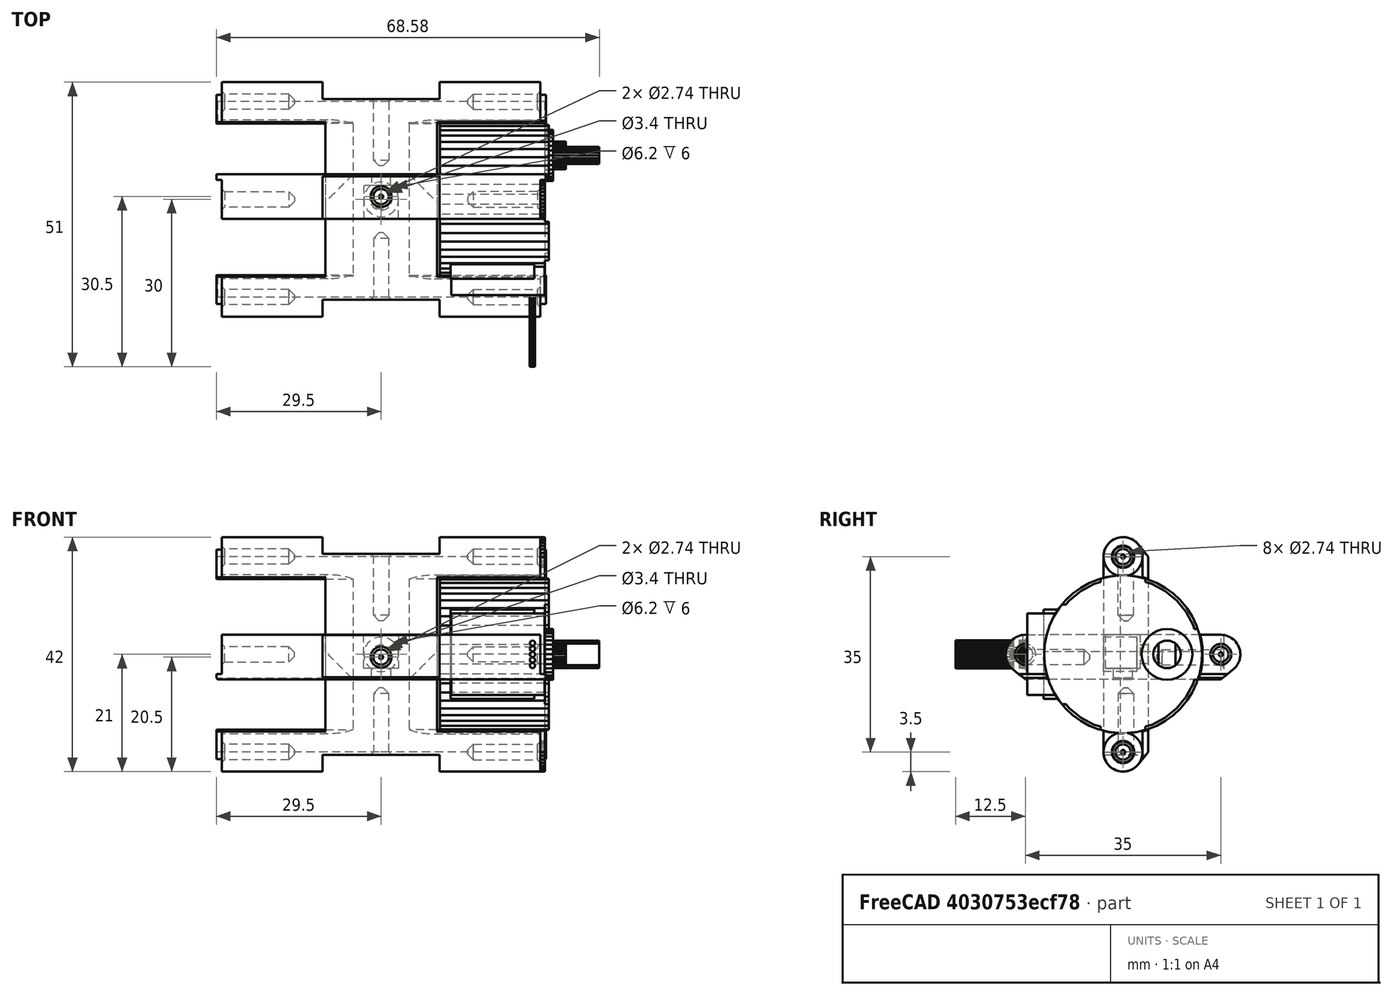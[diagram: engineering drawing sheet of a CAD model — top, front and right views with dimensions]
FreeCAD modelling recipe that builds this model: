
FCSTD DOCUMENT  (FreeCAD 0.17R10654 (Git))
Label: motor-bracket-ng
License: The MIT License
LicenseURL: http://opensource.org/licenses/MIT
objects: Sketcher::SketchObject×9, PartDesign::Pocket×8, PartDesign::Chamfer×3, PartDesign::Body×2, Part::FeaturePython×2, Part::Feature×1, PartDesign::Pad×1, App::DocumentObjectGroup×1, Mesh::Feature×1, Part::Mirroring×1, Part::MultiFuse×1, App::Part×1, Part::Chamfer×1
note: 38 computed .brp shape members not serialized (recipe doc carries the construction recipe); baked Part::Feature solids carry a one-line shape summary decoded from their .brp

FEATURE [Part::Feature] Part__Feature  label="stepper-motor"
  Placement = pos=(19.925,0,0) rot=(0.57735,0.57735,0.57735;2.0944rad)
  shape: bbox 28.55 x 44.13 x 42 mm, 425 faces (baked)
FEATURE [Sketcher::SketchObject] Sketch  label="bracket-sketch"
  MapMode = 5
  Placement = pos=(0,0,0) rot=(0.57735,0.57735,0.57735;2.0944rad)
  Support = -> [YZ_Plane001]
  sketch-geometry (6):
    g0: ArcOfCircle CenterX=0 CenterY=17.5 CenterZ=0 NormalX=0 NormalY=0 NormalZ=1 Radius=3.5 StartAngle=0.679674 EndAngle=3.14159
    g1: ArcOfCircle CenterX=0 CenterY=-17.5 CenterZ=0 NormalX=0 NormalY=0 NormalZ=1 Radius=3.5 StartAngle=3.14159 EndAngle=5.60352
    g2: LineSegment StartX=-3.5 StartY=17.5 StartZ=0 EndX=-3.5 EndY=-17.5 EndZ=0
    g3: LineSegment StartX=4.5 StartY=17.5 StartZ=0 EndX=4.5 EndY=-17.5 EndZ=0
    g4: LineSegment StartX=4.5 StartY=17.5 StartZ=0 EndX=2.72222 EndY=19.6999 EndZ=0
    g5: LineSegment StartX=2.72223 StartY=-19.6999 StartZ=0 EndX=4.5 EndY=-17.5 EndZ=0
  constraints (19):
    c: Tangent(g0,g2)
    c: Tangent(g1,g2)
    c: Coincident(g0,g2)
    c: Coincident(g2,g1)
    c: Vertical(g2)
    c: Radius(g1) = 3.5
    c: PointOnObject(g1,g-2)
    c: DistanceY(g0,g1) = -35
    c: Symmetric(g1,g0,g-1)
    c: Vertical(g3)
    c: Coincident(g3,g4)
    c: Coincident(g0,g4)
    c: Tangent(g0,g4)
    c: DistanceX(g3,g1) = -8
    c: DistanceY(g3) = -35
    c: Symmetric(g3,g3,g-1)
    c: Coincident(g5,g1)
    c: Coincident(g5,g3)
    c: Tangent(g1,g5)
FEATURE [PartDesign::Pad] Pad  label="bracket-pad"
  Length = 29.5
  Length2 = 100
  Placement = pos=(0,0,0) rot=(0.57735,0.57735,0.57735;2.0944rad)
  Profile = -> Sketch
  Type = 0
FEATURE [Sketcher::SketchObject] Sketch001  label="motor-sketch"
  MapMode = 5
  Placement = pos=(29.5,0,0) rot=(0.57735,0.57735,0.57735;2.0944rad)
  Support = -> [Pad]
  sketch-geometry (1):
    g0: Circle CenterX=0 CenterY=0 CenterZ=0 NormalX=0 NormalY=0 NormalZ=1 Radius=14.25
  constraints (2):
    c: Coincident(g0,g-1)
    c: Radius(g0) = 14.25
FEATURE [PartDesign::Pocket] Pocket  label="motor-pocket"
  BaseFeature = -> Pad
  Length = 19.5
  Placement = pos=(0,0,0) rot=(0.57735,0.57735,0.57735;2.0944rad)
  Profile = -> Sketch001
  Type = 0
FEATURE [Sketcher::SketchObject] Sketch002  label="motor-screw-holes-sketch"
  MapMode = 5
  Placement = pos=(29.5,0,0) rot=(0.57735,0.57735,0.57735;2.0944rad)
  Support = -> [Pocket]
  sketch-geometry (2):
    g0: Circle CenterX=0 CenterY=-17.5 CenterZ=0 NormalX=0 NormalY=0 NormalZ=1 Radius=1.37
    g1: Circle CenterX=0 CenterY=17.5 CenterZ=0 NormalX=0 NormalY=0 NormalZ=1 Radius=1.37
  constraints (6):
    c: PointOnObject(g0,g-2)
    c: DistanceY(g-1,g0) = -17.5
    c: Radius(g0) = 1.37
    c: PointOnObject(g1,g-2)
    c: DistanceY(g-1,g1) = 17.5
    c: Radius(g1) = 1.37
FEATURE [PartDesign::Pocket] Pocket001  label="motor-screw-holes-pocket"
  BaseFeature = -> Pocket
  Length = 14
  Placement = pos=(0,0,0) rot=(0.57735,0.57735,0.57735;2.0944rad)
  Profile = -> Sketch002
  Type = 0
FEATURE [Sketcher::SketchObject] Sketch003  label="recess-sketch"
  MapMode = 5
  Placement = pos=(0,-3.5,0) rot=(0.57735,0.57735,-0.57735;2.0944rad)
  Support = -> [Pocket001]
  sketch-geometry (8):
    g0: LineSegment StartX=-22 StartY=10.5 StartZ=0 EndX=-18 EndY=10.5 EndZ=0
    g1: LineSegment StartX=-18 StartY=10.5 StartZ=0 EndX=-18 EndY=0 EndZ=0
    g2: LineSegment StartX=-18 StartY=0 StartZ=0 EndX=-22 EndY=0 EndZ=0
    g3: LineSegment StartX=-22 StartY=0 StartZ=0 EndX=-22 EndY=10.5 EndZ=0
    g4: LineSegment StartX=18 StartY=10.5 StartZ=0 EndX=22 EndY=10.5 EndZ=0
    g5: LineSegment StartX=22 StartY=10.5 StartZ=0 EndX=22 EndY=0 EndZ=0
    g6: LineSegment StartX=22 StartY=0 StartZ=0 EndX=18 EndY=0 EndZ=0
    g7: LineSegment StartX=18 StartY=0 StartZ=0 EndX=18 EndY=10.5 EndZ=0
  constraints (24):
    c: Coincident(g0,g1)
    c: Coincident(g1,g2)
    c: Coincident(g2,g3)
    c: Coincident(g3,g0)
    c: Horizontal(g0)
    c: Horizontal(g2)
    c: Vertical(g1)
    c: Vertical(g3)
    c: PointOnObject(g1,g-1)
    c: DistanceX(g-1,g1) = -18
    c: DistanceX(g2) = -4
    c: DistanceY(g1) = -10.5
    c: Coincident(g4,g5)
    c: Coincident(g5,g6)
    c: Coincident(g6,g7)
    c: Coincident(g7,g4)
    c: Horizontal(g4)
    c: Horizontal(g6)
    c: Vertical(g5)
    c: Vertical(g7)
    c: PointOnObject(g6,g-1)
    c: DistanceY(g7) = 10.5
    c: DistanceX(g6) = -4
    c: DistanceX(g-1,g6) = 18
FEATURE [PartDesign::Pocket] Pocket002  label="recess-pocket"
  BaseFeature = -> Pocket001
  Length = 8
  Placement = pos=(0,0,0) rot=(0.57735,0.57735,0.57735;2.0944rad)
  Profile = -> Sketch003
  Type = 0
FEATURE [App::DocumentObjectGroup] Group  label="components"
  Group = -> [Part__Feature]
FEATURE [Mesh::Feature] _1_motor_bracket  label="01-motor-bracket"
FEATURE [Sketcher::SketchObject] Sketch008
  MapMode = 5
  Placement = pos=(29.5,0,0) rot=(0.57735,0.57735,0.57735;2.0944rad)
  Support = -> [Pocket]
  sketch-geometry (4):
    g0: LineSegment StartX=-3.5 StartY=21 StartZ=0 EndX=3.5 EndY=21 EndZ=0
    g1: LineSegment StartX=3.5 StartY=21 StartZ=0 EndX=3.5 EndY=-21 EndZ=0
    g2: LineSegment StartX=3.5 StartY=-21 StartZ=0 EndX=-3.5 EndY=-21 EndZ=0
    g3: LineSegment StartX=-3.5 StartY=-21 StartZ=0 EndX=-3.5 EndY=21 EndZ=0
  constraints (11):
    c: Coincident(g0,g1)
    c: Coincident(g1,g2)
    c: Coincident(g2,g3)
    c: Coincident(g3,g0)
    c: Horizontal(g0)
    c: Horizontal(g2)
    c: Vertical(g1)
    c: Vertical(g3)
    c: Symmetric(g2,g0,g-1)
    c: DistanceX(g0,g0) = 7
    c: DistanceY(g3,g3) = 42
FEATURE [PartDesign::Pocket] Pocket007
  BaseFeature = -> Pocket002
  Length = 1
  Placement = pos=(0,0,0) rot=(0.57735,0.57735,0.57735;2.0944rad)
  Profile = -> Sketch008
  Type = 0
FEATURE [PartDesign::Body] Pocket002Body
  Group = -> [Sketch,Pad,Sketch001,Pocket,Sketch002,Pocket001,Sketch003,Pocket002,Sketch008,Pocket007]
  Origin = -> Pocket002BodyOrigin
  Tip = -> Pocket007
FEATURE [Part::Mirroring] Part__Mirroring  label="recess-pocket-mirror"
  Base = (0,0,0)
  Normal = (1,0,0)
  Source = -> Pocket002Body
FEATURE [Part::MultiFuse] Fusion  label="bracket-fusion"
  Shapes = -> [Part__Mirroring,Pocket002Body]
FEATURE [Sketcher::SketchObject] Sketch004  label="center-screw-hole-sketch"
  MapMode = 5
  Placement = pos=(0,-3.5,0) rot=(1,0,0;1.5708rad)
  Support = -> [Fusion]
  sketch-geometry (1):
    g0: Circle CenterX=0 CenterY=0 CenterZ=0 NormalX=0 NormalY=0 NormalZ=1 Radius=1.7
  constraints (2):
    c: Coincident(g0,g-1)
    c: Radius(g0) = 1.7
FEATURE [PartDesign::Pocket] Pocket003  label="center-screw-hole-pocket"
  BaseFeature = -> Fusion
  Length = 8
  Profile = -> Sketch004
  Type = 0
FEATURE [Sketcher::SketchObject] Sketch005  label="center-screw-head-hole-sketch"
  MapMode = 5
  Placement = pos=(0,-3.5,0) rot=(1,0,0;1.5708rad)
  Support = -> [Pocket003]
  sketch-geometry (1):
    g0: Circle CenterX=0 CenterY=0 CenterZ=0 NormalX=0 NormalY=0 NormalZ=1 Radius=3.1
  constraints (2):
    c: Coincident(g0,g-1)
    c: Radius(g0) = 3.1
FEATURE [PartDesign::Pocket] Pocket004  label="center-screw-head-hole-pocket"
  BaseFeature = -> Pocket003
  Length = 6
  Profile = -> Sketch005
  Type = 0
FEATURE [Sketcher::SketchObject] Sketch006  label="top-screw-hole-sketch"
  MapMode = 5
  Placement = pos=(0,0,18) rot=(0,0,1;0rad)
  Support = -> [Pocket004]
  sketch-geometry (1):
    g0: Circle CenterX=0 CenterY=0.5 CenterZ=0 NormalX=0 NormalY=0 NormalZ=1 Radius=1.37
  constraints (3):
    c: PointOnObject(g0,g-2)
    c: DistanceY(g-1,g0) = 0.5
    c: Radius(g0) = 1.37
FEATURE [PartDesign::Pocket] Pocket005  label="top-screw-hole-pocket"
  BaseFeature = -> Pocket004
  Length = 12
  Profile = -> Sketch006
  Type = 0
FEATURE [Sketcher::SketchObject] Sketch007  label="bottom-screw-hole-sketch"
  MapMode = 5
  Placement = pos=(0,0,-18) rot=(1,0,0;3.14159rad)
  Support = -> [Pocket005]
  sketch-geometry (1):
    g0: Circle CenterX=0 CenterY=-0.5 CenterZ=0 NormalX=0 NormalY=0 NormalZ=1 Radius=1.37
  constraints (3):
    c: PointOnObject(g0,g-2)
    c: DistanceY(g-1,g0) = -0.5
    c: Radius(g0) = 1.37
FEATURE [PartDesign::Pocket] Pocket006  label="bottom-screw-hole-pocket"
  BaseFeature = -> Pocket005
  Length = 12
  Profile = -> Sketch007
  Type = 0
FEATURE [PartDesign::Chamfer] Chamfer
  Base = -> Pocket006 [Face32,Face44,Face45,Face42,Face41,Face31]
  BaseFeature = -> Pocket006
  Size = 1
FEATURE [PartDesign::Chamfer] Chamfer001
  Base = -> Chamfer [Edge87,Edge31,Edge3,Edge45,Edge72,Edge112]
  BaseFeature = -> Chamfer
  Size = 0.5
FEATURE [PartDesign::Chamfer] Chamfer002
  Base = -> Chamfer001 [Edge58,Edge57]
  BaseFeature = -> Chamfer001
  Size = 5
FEATURE [PartDesign::Body] Pocket006Body
  BaseFeature = -> Fusion
  Group = -> [Sketch004,Pocket003,Sketch005,Pocket004,Sketch006,Pocket005,Sketch007,Pocket006,Chamfer,Chamfer001,Chamfer002]
  Origin = -> Pocket006BodyOrigin
  Tip = -> Chamfer002
FEATURE [App::Part] Part
  Group = -> [Pocket002Body,Pocket006Body]
  License = CC BY 3.0
  LicenseURL = http://creativecommons.org/licenses/by/3.0/
  Origin = -> PartOrigin
FEATURE [Part::FeaturePython] Clone  label="Pocket006Body001"  # Draft clone (typed FeaturePython)
  AttacherType = Attacher::AttachEngine3D
  Objects = -> [Pocket006Body]
  Scale = (1,1,1)
FEATURE [Part::FeaturePython] Clone001  label="Pocket006Body002"  # Draft clone (typed FeaturePython)
  AttacherType = Attacher::AttachEngine3D
  Objects = -> [Pocket006Body]
  Placement = pos=(0,0,0) rot=(-1,0,0;1.5708rad)
  Scale = (1,1,1)
FEATURE [Part::Chamfer] Chamfer003
  Base = -> Clone001
  Edges = 9 edges r=0.25: [Edge2,Edge4,Edge7,Edge8,Edge9,Edge10,Edge13,Edge15,Edge17]
